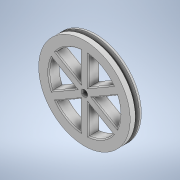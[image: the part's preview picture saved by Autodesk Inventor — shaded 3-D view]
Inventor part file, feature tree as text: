
AUTODESK INVENTOR PART (.ipt)
format: ipt  version: 2020 (Build 240168000, 168)  size: 544,256 bytes
history: native  units: mm
features: extrude x4, sketch x4, other x1, fillet x1, chamfer x1
ambient origin geometry x8: Origin, YZ Plane, XZ Plane, XY Plane, X Axis, Y Axis, Z Axis, Center Point
bodies: Body1 (feature_tree)
feature tree (11):
  other  "솔리드1"
  extrude  "돌출1"  Depth=90.0mm
  extrude  "돌출2"  Depth=3.0mm TaperAngle=0.0deg
  extrude  "돌출3"  Depth=75.0mm
  extrude  "돌출4"  Depth=3.0mm TaperAngle=0.0deg
  fillet  "모깎기2"  Radius=90.0mm
  chamfer  "모따기1"  Distance=5.0mm
  sketch  "스케치1"
  sketch  "스케치2"
  sketch  "스케치3"
  sketch  "스케치4"
